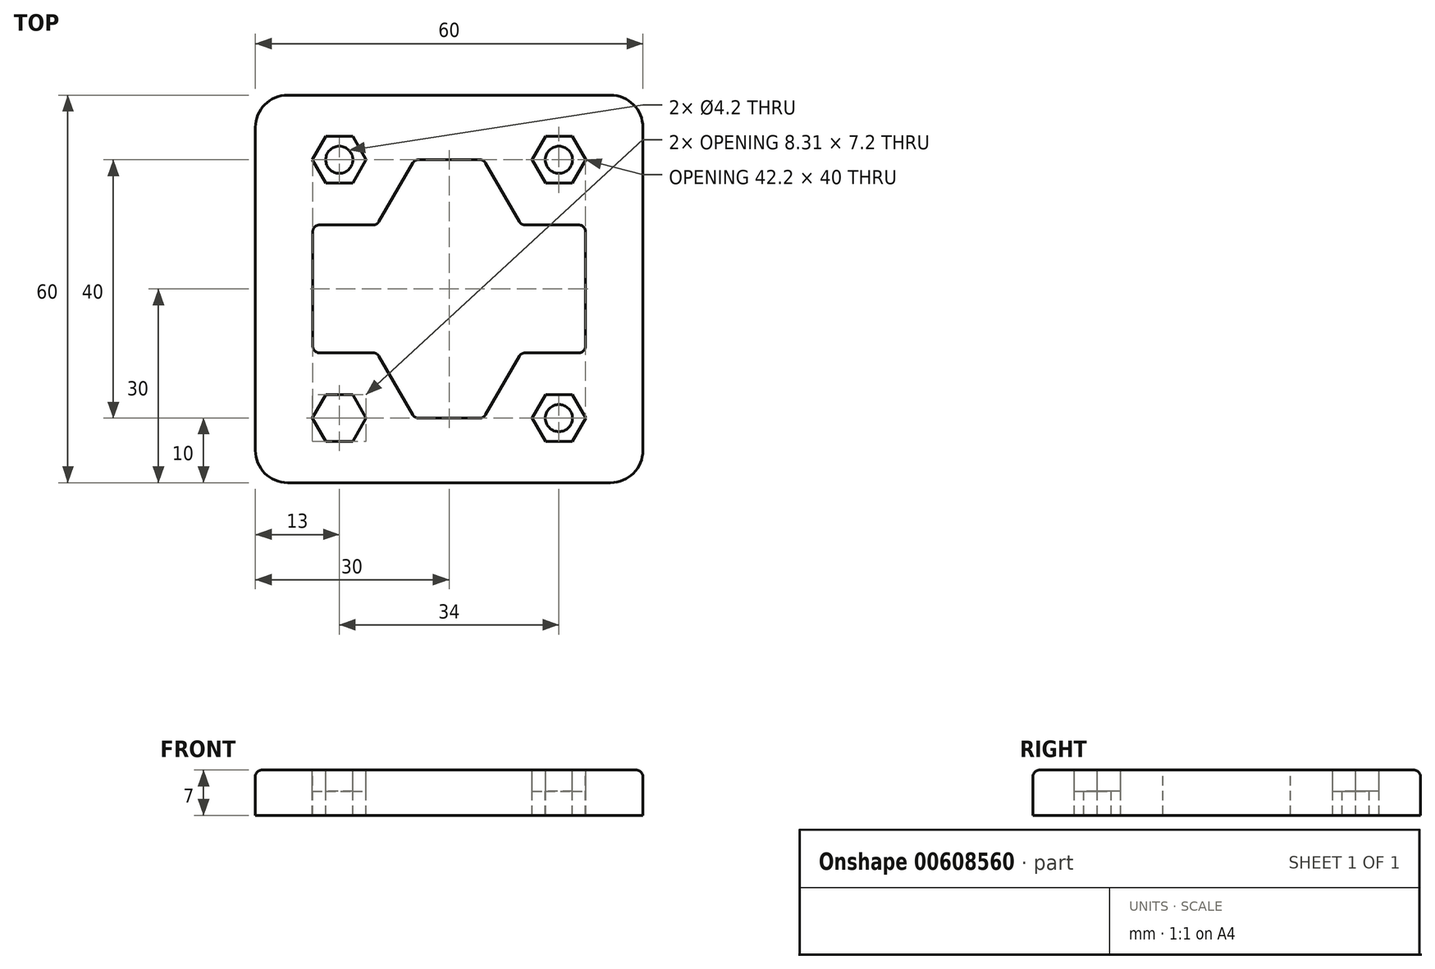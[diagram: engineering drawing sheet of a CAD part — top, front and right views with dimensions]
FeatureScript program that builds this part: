
annotation { "Feature Type Name" : "Feature", "Feature Type Description" : "" }
export const myFeature = defineFeature(function(context is Context, id is Id, definition is map)
    precondition{}
    {
        {
            var Q0;
            Q0=qCreatedBy(makeId("Top.planeOp"),FACE);
            var sketch = newSketch(context, id + "F0", { "sketchPlane" : qUnion([Q0])});
            skLineSegment(sketch, "E0.bottom", {"start": v(30, 30) * mm, "end": v(-30, 30) * mm});
            skLineSegment(sketch, "E0.top", {"start": v(30, -30) * mm, "end": v(-30, -30) * mm});
            skLineSegment(sketch, "E0.left", {"start": v(30, 30) * mm, "end": v(30, -30) * mm});
            skLineSegment(sketch, "E0.right", {"start": v(-30, 30) * mm, "end": v(-30, -30) * mm});
            skPoint(sketch, "E0.middle", {"position": v(0, 0) * mm});
            skSolve(sketch);
        }
        {
            var Q0;
            Q0=makeQuery(id+"F0.imprint","IMPRINT",FACE,{"disambiguationData":[TD([[makeQuery(id+"F0.imprint","IMPRINT",EDGE,{"derivedFrom":sQuery(id+"F0.wireOp",EDGE,"E0.bottom")}),1.0]])]});
            extrude(context, id + "F1", {"entities" : qUnion([Q0]), "oppositeDirection" : true, "depth" : 7 * mm, "offsetDistance" : 25 * mm});
        }
        {
            var Q0;
            Q0=makeQuery(id+"F1.opExtrude","SWEPT_EDGE",EDGE,{"disambiguationData":[OSD([sQuery(id+"F0.wireOp",EDGE,"E0.bottom"),sQuery(id+"F0.wireOp",EDGE,"E0.right")])]});
            var Q1;
            Q1=makeQuery(id+"F1.opExtrude","SWEPT_EDGE",EDGE,{"disambiguationData":[OSD([sQuery(id+"F0.wireOp",EDGE,"E0.bottom"),sQuery(id+"F0.wireOp",EDGE,"E0.left")])]});
            var Q2;
            Q2=makeQuery(id+"F1.opExtrude","SWEPT_EDGE",EDGE,{"disambiguationData":[OSD([sQuery(id+"F0.wireOp",EDGE,"E0.top"),sQuery(id+"F0.wireOp",EDGE,"E0.left")])]});
            var Q3;
            Q3=makeQuery(id+"F1.opExtrude","SWEPT_EDGE",EDGE,{"disambiguationData":[OSD([sQuery(id+"F0.wireOp",EDGE,"E0.top"),sQuery(id+"F0.wireOp",EDGE,"E0.right")])]});
            fillet(context, id + "F2", {"entities" : qUnion([Q0, Q1, Q2, Q3]), "radius" : 5 * mm, "tangentPropagation" : true, "allowEdgeOverflow" : false});
        }
        {
            var Q0;
            Q0=makeQuery(id+"F1.opExtrude","CAP_FACE",FACE,{"disambiguationData":[OSD([sQuery(id+"F0.wireOp",EDGE,"E0.bottom"),sQuery(id+"F0.wireOp",EDGE,"E0.top"),sQuery(id+"F0.wireOp",EDGE,"E0.left"),sQuery(id+"F0.wireOp",EDGE,"E0.right")])],"isStart":true});
            var sketch = newSketch(context, id + "F3", { "sketchPlane" : qUnion([Q0])});
            skLineSegment(sketch, "E1", {"start": v(0, 0) * mm, "end": v(0, 20) * mm, "construction": true});
            skLineSegment(sketch, "E2", {"start": v(0, 20) * mm, "end": v(-17, 20) * mm, "construction": true});
            skCircle(sketch, "E3", {"center": v(-17, 20) * mm, "radius": 2.1 * mm});
            skCircle(sketch, "E4.MirrorC", {"center": v(17, 20) * mm, "radius": 2.1 * mm});
            skCircle(sketch, "E5.MirrorC", {"center": v(-17, -20) * mm, "radius": 2.1 * mm});
            skCircle(sketch, "E6.MirrorC", {"center": v(17, -20) * mm, "radius": 2.1 * mm});
            skLineSegment(sketch, "E7.0", {"start": v(-6.2, 18.5) * mm, "end": v(-10.3, 11.4) * mm});
            skLineSegment(sketch, "E8", {"start": v(-6.2, 18.5) * mm, "end": v(-5.34, 20) * mm});
            skLineSegment(sketch, "E9.0", {"start": v(-12.9, 9.9) * mm, "end": v(-21.1, 9.9) * mm});
            skLineSegment(sketch, "E10", {"start": v(-10.3, 11.4) * mm, "end": v(-11.17, 9.9) * mm});
            skLineSegment(sketch, "E11", {"start": v(-11.17, 9.9) * mm, "end": v(-12.9, 9.9) * mm});
            skLineSegment(sketch, "E12", {"start": v(-21.1, 9.9) * mm, "end": v(-25.2, 9.9) * mm});
            skLineSegment(sketch, "E13", {"start": v(-25.2, 9.9) * mm, "end": v(-25.2, 0) * mm});
            skLineSegment(sketch, "E14", {"start": v(-5.34, 20) * mm, "end": v(0, 20) * mm});
            skLineSegment(sketch, "E15", {"start": v(0, 20) * mm, "end": v(-5.34, 20) * mm});
            skLineSegment(sketch, "E16.MirrorCS", {"start": v(6.2, 18.5) * mm, "end": v(5.34, 20) * mm});
            skLineSegment(sketch, "E17.MirrorCS", {"start": v(6.2, 18.5) * mm, "end": v(10.3, 11.4) * mm});
            skLineSegment(sketch, "E18.MirrorCS", {"start": v(10.3, 11.4) * mm, "end": v(11.17, 9.9) * mm});
            skLineSegment(sketch, "E19.MirrorCS", {"start": v(11.17, 9.9) * mm, "end": v(12.9, 9.9) * mm});
            skLineSegment(sketch, "E20.MirrorCS", {"start": v(12.9, 9.9) * mm, "end": v(21.1, 9.9) * mm});
            skLineSegment(sketch, "E21.MirrorCS", {"start": v(21.1, 9.9) * mm, "end": v(25.2, 9.9) * mm});
            skLineSegment(sketch, "E22.MirrorCS", {"start": v(25.2, 9.9) * mm, "end": v(25.2, 0) * mm});
            skLineSegment(sketch, "E23.MirrorCS", {"start": v(-25.2, -9.9) * mm, "end": v(-25.2, 0) * mm});
            skLineSegment(sketch, "E24.MirrorCS", {"start": v(-21.1, -9.9) * mm, "end": v(-25.2, -9.9) * mm});
            skLineSegment(sketch, "E25.MirrorCS", {"start": v(-12.9, -9.9) * mm, "end": v(-21.1, -9.9) * mm});
            skLineSegment(sketch, "E26.MirrorCS", {"start": v(-11.17, -9.9) * mm, "end": v(-12.9, -9.9) * mm});
            skLineSegment(sketch, "E27.MirrorCS", {"start": v(-10.3, -11.4) * mm, "end": v(-11.17, -9.9) * mm});
            skLineSegment(sketch, "E28.MirrorCS", {"start": v(-6.2, -18.5) * mm, "end": v(-10.3, -11.4) * mm});
            skLineSegment(sketch, "E29.MirrorCS", {"start": v(-6.2, -18.5) * mm, "end": v(-5.34, -20) * mm});
            skLineSegment(sketch, "E30.MirrorCS", {"start": v(6.2, -18.5) * mm, "end": v(5.34, -20) * mm});
            skLineSegment(sketch, "E31.MirrorCS", {"start": v(6.2, -18.5) * mm, "end": v(10.3, -11.4) * mm});
            skLineSegment(sketch, "E32.MirrorCS", {"start": v(10.3, -11.4) * mm, "end": v(11.17, -9.9) * mm});
            skLineSegment(sketch, "E33.MirrorCS", {"start": v(11.17, -9.9) * mm, "end": v(12.9, -9.9) * mm});
            skLineSegment(sketch, "E34.MirrorCS", {"start": v(12.9, -9.9) * mm, "end": v(21.1, -9.9) * mm});
            skLineSegment(sketch, "E35.MirrorCS", {"start": v(21.1, -9.9) * mm, "end": v(25.2, -9.9) * mm});
            skLineSegment(sketch, "E36.MirrorCS", {"start": v(25.2, -9.9) * mm, "end": v(25.2, 0) * mm});
            skLineSegment(sketch, "E37", {"start": v(-5.34, 20) * mm, "end": v(5.34, 20) * mm});
            skLineSegment(sketch, "E38", {"start": v(5.34, -20) * mm, "end": v(-5.34, -20) * mm});
            skLineSegment(sketch, "E39", {"start": v(-21.1, 9.9) * mm, "end": v(-21.1, -9.9) * mm});
            skLineSegment(sketch, "E40", {"start": v(21.1, 9.9) * mm, "end": v(21.1, -9.9) * mm});
            skLineSegment(sketch, "E41", {"start": v(-17, 23.6) * mm, "end": v(-17, 16.4) * mm});
            skCircle(sketch, "E42.cCircle", {"center": v(-17, 20) * mm, "radius": 3.6 * mm, "construction": true});
            skLineSegment(sketch, "E42.0", {"start": v(-19.08, 23.6) * mm, "end": v(-14.92, 23.6) * mm});
            skLineSegment(sketch, "E42.1", {"start": v(-14.92, 23.6) * mm, "end": v(-12.84, 20) * mm});
            skLineSegment(sketch, "E42.2", {"start": v(-12.84, 20) * mm, "end": v(-14.92, 16.4) * mm});
            skLineSegment(sketch, "E42.3", {"start": v(-14.92, 16.4) * mm, "end": v(-19.08, 16.4) * mm});
            skLineSegment(sketch, "E42.4", {"start": v(-19.08, 16.4) * mm, "end": v(-21.16, 20) * mm});
            skLineSegment(sketch, "E42.5", {"start": v(-21.16, 20) * mm, "end": v(-19.08, 23.6) * mm});
            skPoint(sketch, "E42.0.midPoint", {"position": v(-17, 23.6) * mm});
            skLineSegment(sketch, "E43.MirrorCS", {"start": v(14.92, 23.6) * mm, "end": v(12.84, 20) * mm});
            skLineSegment(sketch, "E44.MirrorCS", {"start": v(19.08, 23.6) * mm, "end": v(14.92, 23.6) * mm});
            skLineSegment(sketch, "E45.MirrorCS", {"start": v(21.16, 20) * mm, "end": v(19.08, 23.6) * mm});
            skLineSegment(sketch, "E46.MirrorCS", {"start": v(19.08, 16.4) * mm, "end": v(21.16, 20) * mm});
            skLineSegment(sketch, "E47.MirrorCS", {"start": v(14.92, 16.4) * mm, "end": v(19.08, 16.4) * mm});
            skLineSegment(sketch, "E48.MirrorCS", {"start": v(12.84, 20) * mm, "end": v(14.92, 16.4) * mm});
            skLineSegment(sketch, "E49.MirrorCS", {"start": v(-19.08, -23.6) * mm, "end": v(-14.92, -23.6) * mm});
            skLineSegment(sketch, "E50.MirrorCS", {"start": v(-21.16, -20) * mm, "end": v(-19.08, -23.6) * mm});
            skLineSegment(sketch, "E51.MirrorCS", {"start": v(-12.84, -20) * mm, "end": v(-14.92, -16.4) * mm});
            skLineSegment(sketch, "E52.MirrorCS", {"start": v(-14.92, -16.4) * mm, "end": v(-19.08, -16.4) * mm});
            skLineSegment(sketch, "E53.MirrorCS", {"start": v(-17, -23.6) * mm, "end": v(-17, -16.4) * mm});
            skLineSegment(sketch, "E54.MirrorCS", {"start": v(-19.08, -16.4) * mm, "end": v(-21.16, -20) * mm});
            skPoint(sketch, "E55.MirrorP", {"position": v(-17, -23.6) * mm});
            skCircle(sketch, "E56.MirrorC", {"center": v(-17, -20) * mm, "radius": 3.6 * mm, "construction": true});
            skLineSegment(sketch, "E57.MirrorCS", {"start": v(-14.92, -23.6) * mm, "end": v(-12.84, -20) * mm});
            skLineSegment(sketch, "E58.MirrorCS", {"start": v(21.16, -20) * mm, "end": v(19.08, -23.6) * mm});
            skLineSegment(sketch, "E59.MirrorCS", {"start": v(19.08, -16.4) * mm, "end": v(21.16, -20) * mm});
            skLineSegment(sketch, "E60.MirrorCS", {"start": v(12.84, -20) * mm, "end": v(14.92, -16.4) * mm});
            skLineSegment(sketch, "E61.MirrorCS", {"start": v(14.92, -23.6) * mm, "end": v(12.84, -20) * mm});
            skLineSegment(sketch, "E62.MirrorCS", {"start": v(14.92, -16.4) * mm, "end": v(19.08, -16.4) * mm});
            skLineSegment(sketch, "E63.MirrorCS", {"start": v(19.08, -23.6) * mm, "end": v(14.92, -23.6) * mm});
            skSolve(sketch);
        }
        {
            var Q0;
            Q0=makeQuery(id+"F3.imprint","IMPRINT",FACE,{"disambiguationData":[TD([[makeQuery(id+"F3.imprint","IMPRINT",EDGE,{"derivedFrom":sQuery(id+"F3.wireOp",EDGE,"E3")}),1.0]])]});
            var Q1;
            Q1=makeQuery(id+"F3.imprint","IMPRINT",FACE,{"disambiguationData":[TD([[makeQuery(id+"F3.imprint","IMPRINT",EDGE,{"derivedFrom":sQuery(id+"F3.wireOp",EDGE,"E4.MirrorC")}),-1.0]])]});
            var Q2;
            Q2=makeQuery(id+"F3.imprint","IMPRINT",FACE,{"disambiguationData":[TD([[makeQuery(id+"F3.imprint","IMPRINT",EDGE,{"derivedFrom":sQuery(id+"F3.wireOp",EDGE,"E6.MirrorC")}),1.0]])]});
            var Q3;
            Q3=makeQuery(id+"F3.imprint","IMPRINT",FACE,{"disambiguationData":[TD([[makeQuery(id+"F3.imprint","IMPRINT",EDGE,{"derivedFrom":sQuery(id+"F3.wireOp",EDGE,"E5.MirrorC")}),-1.0]])]});
            var Q4;
            {var subQ0=sQuery(id+"F3.wireOp",EDGE,"E5.MirrorC");var subQ1=sQuery(id+"F3.wireOp",EDGE,"E53.MirrorCS");var subQ2=makeQuery(id+"F3.imprint","INTERSECT",VERTEX,{"disambiguationData":[OD(0.0)],"derivedFrom":[subQ1,subQ0]});Q4=makeQuery(id+"F3.imprint","IMPRINT",FACE,{"disambiguationData":[TD([[makeQuery(id+"F3.imprint","IMPRINT",EDGE,{"disambiguationData":[TD([[subQ2,-1.0]])],"derivedFrom":subQ1}),1.0]])]});}
            var Q5;
            {var subQ0=sQuery(id+"F3.wireOp",EDGE,"E5.MirrorC");var subQ1=sQuery(id+"F3.wireOp",EDGE,"E53.MirrorCS");var subQ2=makeQuery(id+"F3.imprint","INTERSECT",VERTEX,{"disambiguationData":[OD(0.0)],"derivedFrom":[subQ1,subQ0]});Q5=makeQuery(id+"F3.imprint","IMPRINT",FACE,{"disambiguationData":[TD([[makeQuery(id+"F3.imprint","IMPRINT",EDGE,{"disambiguationData":[TD([[subQ2,-1.0]])],"derivedFrom":subQ1}),-1.0]])]});}
            var Q6;
            Q6=makeQuery(id+"F3.imprint","IMPRINT",FACE,{"disambiguationData":[TD([[makeQuery(id+"F3.imprint","IMPRINT",EDGE,{"derivedFrom":sQuery(id+"F3.wireOp",EDGE,"E6.MirrorC")}),1.0]])]});
            extrude(context, id + "F4", {"entities" : qUnion([Q0, Q1, Q2, Q3, Q4, Q5, Q6]), "operationType" : NewBodyOperationType.REMOVE, "oppositeDirection" : true, "depth" : 25 * mm, "offsetDistance" : 25 * mm});
        }
        {
            var Q0;
            Q0=makeQuery(id+"F3.imprint","IMPRINT",FACE,{"disambiguationData":[TD([[makeQuery(id+"F3.imprint","IMPRINT",EDGE,{"derivedFrom":sQuery(id+"F3.wireOp",EDGE,"E3")}),-1.0]])]});
            var Q1;
            Q1=makeQuery(id+"F3.imprint","IMPRINT",FACE,{"disambiguationData":[TD([[makeQuery(id+"F3.imprint","IMPRINT",EDGE,{"derivedFrom":sQuery(id+"F3.wireOp",EDGE,"E4.MirrorC")}),1.0]])]});
            var Q2;
            Q2=makeQuery(id+"F3.imprint","IMPRINT",FACE,{"disambiguationData":[TD([[makeQuery(id+"F3.imprint","IMPRINT",EDGE,{"derivedFrom":sQuery(id+"F3.wireOp",EDGE,"297063ce-58de-4e23-9618-ebe68274b3f90.MirrorCS")}),-1.0]])]});
            var Q3;
            Q3=makeQuery(id+"F3.imprint","IMPRINT",FACE,{"disambiguationData":[TD([[makeQuery(id+"F3.imprint","IMPRINT",EDGE,{"derivedFrom":sQuery(id+"F3.wireOp",EDGE,"11c745cf-a508-4151-a166-093f8a6f8d340.MirrorCS")}),1.0]])]});
            var Q4;
            {var subQ5=sQuery(id+"F3.wireOp",EDGE,"E50.MirrorCS");Q4=makeQuery(id+"F3.imprint","IMPRINT",FACE,{"disambiguationData":[TD([[makeQuery(id+"F3.imprint","IMPRINT",EDGE,{"derivedFrom":subQ5}),1.0]])]});}
            var Q5;
            {var subQ1=sQuery(id+"F3.wireOp",EDGE,"E51.MirrorCS");Q5=makeQuery(id+"F3.imprint","IMPRINT",FACE,{"disambiguationData":[TD([[makeQuery(id+"F3.imprint","IMPRINT",EDGE,{"derivedFrom":subQ1}),1.0]])]});}
            var Q6;
            Q6=makeQuery(id+"F3.imprint","IMPRINT",FACE,{"disambiguationData":[TD([[makeQuery(id+"F3.imprint","IMPRINT",EDGE,{"derivedFrom":sQuery(id+"F3.wireOp",EDGE,"E58.MirrorCS")}),-1.0]])]});
            extrude(context, id + "F5", {"entities" : qUnion([Q0, Q1, Q2, Q3, Q4, Q5, Q6]), "operationType" : NewBodyOperationType.REMOVE, "oppositeDirection" : true, "depth" : 3.3 * mm, "offsetDistance" : 25 * mm});
        }
        {
            var Q0;
            Q0=makeQuery(id+"F1.opExtrude","CAP_EDGE",EDGE,{"disambiguationData":[OSD([sQuery(id+"F0.wireOp",EDGE,"E0.left")])],"isStart":true});
            var Q1;
            Q1=makeQuery(id+"F1.opExtrude","CAP_EDGE",EDGE,{"disambiguationData":[OSD([sQuery(id+"F0.wireOp",EDGE,"E0.bottom")])],"isStart":true});
            var Q2;
            Q2=makeQuery(id+"F1.opExtrude","CAP_EDGE",EDGE,{"disambiguationData":[OSD([sQuery(id+"F0.wireOp",EDGE,"E0.right")])],"isStart":true});
            var Q3;
            Q3=makeQuery(id+"F1.opExtrude","CAP_EDGE",EDGE,{"disambiguationData":[OSD([sQuery(id+"F0.wireOp",EDGE,"E0.top")])],"isStart":true});
            var Q4;
            {var subQ0=sQuery(id+"F0.wireOp",EDGE,"E0.right");var subQ1=sQuery(id+"F0.wireOp",EDGE,"E0.top");Q4=makeQuery(id+"F2.opFillet","BLEND_EDGE",EDGE,{"blendedFrom":[makeQuery(id+"F1.opExtrude","SWEPT_EDGE",EDGE,{"disambiguationData":[OSD([subQ1,subQ0])]}),makeQuery(id+"F1.opExtrude","CAP_FACE",FACE,{"disambiguationData":[OSD([sQuery(id+"F0.wireOp",EDGE,"E0.bottom"),subQ1,sQuery(id+"F0.wireOp",EDGE,"E0.left"),subQ0])],"isStart":true})],"blendedInto":[makeQuery(id+"F1.opExtrude","CAP_FACE",FACE,{"disambiguationData":[OSD([sQuery(id+"F0.wireOp",EDGE,"E0.bottom"),subQ1,sQuery(id+"F0.wireOp",EDGE,"E0.left"),subQ0])],"isStart":true})]});}
            var Q5;
            {var subQ0=sQuery(id+"F0.wireOp",EDGE,"E0.left");var subQ1=sQuery(id+"F0.wireOp",EDGE,"E0.top");Q5=makeQuery(id+"F2.opFillet","BLEND_EDGE",EDGE,{"blendedFrom":[makeQuery(id+"F1.opExtrude","SWEPT_EDGE",EDGE,{"disambiguationData":[OSD([subQ1,subQ0])]}),makeQuery(id+"F1.opExtrude","CAP_FACE",FACE,{"disambiguationData":[OSD([sQuery(id+"F0.wireOp",EDGE,"E0.bottom"),subQ1,subQ0,sQuery(id+"F0.wireOp",EDGE,"E0.right")])],"isStart":true})],"blendedInto":[makeQuery(id+"F1.opExtrude","CAP_FACE",FACE,{"disambiguationData":[OSD([sQuery(id+"F0.wireOp",EDGE,"E0.bottom"),subQ1,subQ0,sQuery(id+"F0.wireOp",EDGE,"E0.right")])],"isStart":true})]});}
            var Q6;
            {var subQ0=sQuery(id+"F0.wireOp",EDGE,"E0.left");var subQ1=sQuery(id+"F0.wireOp",EDGE,"E0.bottom");Q6=makeQuery(id+"F2.opFillet","BLEND_EDGE",EDGE,{"blendedFrom":[makeQuery(id+"F1.opExtrude","SWEPT_EDGE",EDGE,{"disambiguationData":[OSD([subQ1,subQ0])]}),makeQuery(id+"F1.opExtrude","CAP_FACE",FACE,{"disambiguationData":[OSD([subQ1,sQuery(id+"F0.wireOp",EDGE,"E0.top"),subQ0,sQuery(id+"F0.wireOp",EDGE,"E0.right")])],"isStart":true})],"blendedInto":[makeQuery(id+"F1.opExtrude","CAP_FACE",FACE,{"disambiguationData":[OSD([subQ1,sQuery(id+"F0.wireOp",EDGE,"E0.top"),subQ0,sQuery(id+"F0.wireOp",EDGE,"E0.right")])],"isStart":true})]});}
            var Q7;
            {var subQ0=sQuery(id+"F0.wireOp",EDGE,"E0.right");var subQ1=sQuery(id+"F0.wireOp",EDGE,"E0.bottom");Q7=makeQuery(id+"F2.opFillet","BLEND_EDGE",EDGE,{"blendedFrom":[makeQuery(id+"F1.opExtrude","SWEPT_EDGE",EDGE,{"disambiguationData":[OSD([subQ1,subQ0])]}),makeQuery(id+"F1.opExtrude","CAP_FACE",FACE,{"disambiguationData":[OSD([subQ1,sQuery(id+"F0.wireOp",EDGE,"E0.top"),sQuery(id+"F0.wireOp",EDGE,"E0.left"),subQ0])],"isStart":true})],"blendedInto":[makeQuery(id+"F1.opExtrude","CAP_FACE",FACE,{"disambiguationData":[OSD([subQ1,sQuery(id+"F0.wireOp",EDGE,"E0.top"),sQuery(id+"F0.wireOp",EDGE,"E0.left"),subQ0])],"isStart":true})]});}
            fillet(context, id + "F6", {"entities" : qUnion([Q0, Q1, Q2, Q3, Q4, Q5, Q6, Q7]), "radius" : 1 * mm, "tangentPropagation" : true, "allowEdgeOverflow" : false});
        }
        {
            var Q0;
            Q0=makeQuery(id+"F3.imprint","IMPRINT",FACE,{"disambiguationData":[TD([[makeQuery(id+"F3.imprint","IMPRINT",EDGE,{"derivedFrom":sQuery(id+"F3.wireOp",EDGE,"E7.0")}),1.0]])]});
            extrude(context, id + "F7", {"entities" : qUnion([Q0]), "operationType" : NewBodyOperationType.REMOVE, "oppositeDirection" : true, "depth" : 25 * mm, "offsetDistance" : 25 * mm});
        }
        {
            var Q0;
            Q0=makeQuery(id+"F7.boolean.opBoolean","COPY",EDGE,{"derivedFrom":makeQuery(id+"F7.opExtrude","CAP_EDGE",EDGE,{"disambiguationData":[OSD([sQuery(id+"F3.wireOp",EDGE,"E9.0"),sQuery(id+"F3.wireOp",EDGE,"E11")])],"isStart":true})});
            var Q1;
            Q1=makeQuery(id+"F7.boolean.opBoolean","COPY",EDGE,{"derivedFrom":makeQuery(id+"F7.opExtrude","CAP_EDGE",EDGE,{"disambiguationData":[OSD([sQuery(id+"F3.wireOp",EDGE,"E39")])],"isStart":true})});
            var Q2;
            Q2=makeQuery(id+"F7.boolean.opBoolean","COPY",EDGE,{"derivedFrom":makeQuery(id+"F7.opExtrude","CAP_EDGE",EDGE,{"disambiguationData":[OSD([sQuery(id+"F3.wireOp",EDGE,"E7.0"),sQuery(id+"F3.wireOp",EDGE,"E8"),sQuery(id+"F3.wireOp",EDGE,"E10")])],"isStart":true})});
            var Q3;
            Q3=makeQuery(id+"F7.boolean.opBoolean","COPY",EDGE,{"derivedFrom":makeQuery(id+"F7.opExtrude","CAP_EDGE",EDGE,{"disambiguationData":[OSD([sQuery(id+"F3.wireOp",EDGE,"E37")])],"isStart":true})});
            var Q4;
            Q4=makeQuery(id+"F7.boolean.opBoolean","COPY",EDGE,{"derivedFrom":makeQuery(id+"F7.opExtrude","CAP_EDGE",EDGE,{"disambiguationData":[OSD([sQuery(id+"F3.wireOp",EDGE,"E16.MirrorCS"),sQuery(id+"F3.wireOp",EDGE,"E17.MirrorCS"),sQuery(id+"F3.wireOp",EDGE,"E18.MirrorCS")])],"isStart":true})});
            var Q5;
            Q5=makeQuery(id+"F7.boolean.opBoolean","COPY",EDGE,{"derivedFrom":makeQuery(id+"F7.opExtrude","CAP_EDGE",EDGE,{"disambiguationData":[OSD([sQuery(id+"F3.wireOp",EDGE,"E19.MirrorCS"),sQuery(id+"F3.wireOp",EDGE,"E20.MirrorCS")])],"isStart":true})});
            var Q6;
            Q6=makeQuery(id+"F7.boolean.opBoolean","COPY",EDGE,{"derivedFrom":makeQuery(id+"F7.opExtrude","CAP_EDGE",EDGE,{"disambiguationData":[OSD([sQuery(id+"F3.wireOp",EDGE,"E40")])],"isStart":true})});
            var Q7;
            Q7=makeQuery(id+"F7.boolean.opBoolean","COPY",EDGE,{"derivedFrom":makeQuery(id+"F7.opExtrude","CAP_EDGE",EDGE,{"disambiguationData":[OSD([sQuery(id+"F3.wireOp",EDGE,"E33.MirrorCS"),sQuery(id+"F3.wireOp",EDGE,"E34.MirrorCS")])],"isStart":true})});
            var Q8;
            Q8=makeQuery(id+"F7.boolean.opBoolean","COPY",EDGE,{"derivedFrom":makeQuery(id+"F7.opExtrude","CAP_EDGE",EDGE,{"disambiguationData":[OSD([sQuery(id+"F3.wireOp",EDGE,"E30.MirrorCS"),sQuery(id+"F3.wireOp",EDGE,"E31.MirrorCS"),sQuery(id+"F3.wireOp",EDGE,"E32.MirrorCS")])],"isStart":true})});
            var Q9;
            Q9=makeQuery(id+"F7.boolean.opBoolean","COPY",EDGE,{"derivedFrom":makeQuery(id+"F7.opExtrude","CAP_EDGE",EDGE,{"disambiguationData":[OSD([sQuery(id+"F3.wireOp",EDGE,"E38")])],"isStart":true})});
            var Q10;
            Q10=makeQuery(id+"F7.boolean.opBoolean","COPY",EDGE,{"derivedFrom":makeQuery(id+"F7.opExtrude","CAP_EDGE",EDGE,{"disambiguationData":[OSD([sQuery(id+"F3.wireOp",EDGE,"E27.MirrorCS"),sQuery(id+"F3.wireOp",EDGE,"E28.MirrorCS"),sQuery(id+"F3.wireOp",EDGE,"E29.MirrorCS")])],"isStart":true})});
            var Q11;
            Q11=makeQuery(id+"F7.boolean.opBoolean","COPY",EDGE,{"derivedFrom":makeQuery(id+"F7.opExtrude","CAP_EDGE",EDGE,{"disambiguationData":[OSD([sQuery(id+"F3.wireOp",EDGE,"E25.MirrorCS"),sQuery(id+"F3.wireOp",EDGE,"E26.MirrorCS")])],"isStart":true})});
            var Q12;
            Q12=makeQuery(id+"F7.boolean.opBoolean","COPY",EDGE,{"derivedFrom":makeQuery(id+"F7.opExtrude","SWEPT_EDGE",EDGE,{"disambiguationData":[OSD([sQuery(id+"F3.wireOp",EDGE,"E10"),sQuery(id+"F3.wireOp",EDGE,"E11")])]})});
            var Q13;
            Q13=makeQuery(id+"F7.boolean.opBoolean","COPY",EDGE,{"derivedFrom":makeQuery(id+"F7.opExtrude","SWEPT_EDGE",EDGE,{"disambiguationData":[OSD([sQuery(id+"F3.wireOp",EDGE,"E8"),sQuery(id+"F3.wireOp",EDGE,"E37")])]})});
            var Q14;
            Q14=makeQuery(id+"F7.boolean.opBoolean","COPY",EDGE,{"derivedFrom":makeQuery(id+"F7.opExtrude","SWEPT_EDGE",EDGE,{"disambiguationData":[OSD([sQuery(id+"F3.wireOp",EDGE,"E16.MirrorCS"),sQuery(id+"F3.wireOp",EDGE,"E37")])]})});
            var Q15;
            Q15=makeQuery(id+"F7.boolean.opBoolean","COPY",EDGE,{"derivedFrom":makeQuery(id+"F7.opExtrude","SWEPT_EDGE",EDGE,{"disambiguationData":[OSD([sQuery(id+"F3.wireOp",EDGE,"E18.MirrorCS"),sQuery(id+"F3.wireOp",EDGE,"E19.MirrorCS")])]})});
            var Q16;
            Q16=makeQuery(id+"F7.boolean.opBoolean","COPY",EDGE,{"derivedFrom":makeQuery(id+"F7.opExtrude","SWEPT_EDGE",EDGE,{"disambiguationData":[OSD([sQuery(id+"F3.wireOp",EDGE,"E20.MirrorCS"),sQuery(id+"F3.wireOp",EDGE,"E21.MirrorCS"),sQuery(id+"F3.wireOp",EDGE,"E40")])]})});
            var Q17;
            Q17=makeQuery(id+"F7.boolean.opBoolean","COPY",EDGE,{"derivedFrom":makeQuery(id+"F7.opExtrude","SWEPT_EDGE",EDGE,{"disambiguationData":[OSD([sQuery(id+"F3.wireOp",EDGE,"E34.MirrorCS"),sQuery(id+"F3.wireOp",EDGE,"E35.MirrorCS"),sQuery(id+"F3.wireOp",EDGE,"E40")])]})});
            var Q18;
            Q18=makeQuery(id+"F7.boolean.opBoolean","COPY",EDGE,{"derivedFrom":makeQuery(id+"F7.opExtrude","SWEPT_EDGE",EDGE,{"disambiguationData":[OSD([sQuery(id+"F3.wireOp",EDGE,"E32.MirrorCS"),sQuery(id+"F3.wireOp",EDGE,"E33.MirrorCS")])]})});
            var Q19;
            Q19=makeQuery(id+"F7.boolean.opBoolean","COPY",EDGE,{"derivedFrom":makeQuery(id+"F7.opExtrude","SWEPT_EDGE",EDGE,{"disambiguationData":[OSD([sQuery(id+"F3.wireOp",EDGE,"E30.MirrorCS"),sQuery(id+"F3.wireOp",EDGE,"E38")])]})});
            var Q20;
            Q20=makeQuery(id+"F7.boolean.opBoolean","COPY",EDGE,{"derivedFrom":makeQuery(id+"F7.opExtrude","SWEPT_EDGE",EDGE,{"disambiguationData":[OSD([sQuery(id+"F3.wireOp",EDGE,"E29.MirrorCS"),sQuery(id+"F3.wireOp",EDGE,"E38")])]})});
            var Q21;
            Q21=makeQuery(id+"F7.boolean.opBoolean","COPY",EDGE,{"derivedFrom":makeQuery(id+"F7.opExtrude","SWEPT_EDGE",EDGE,{"disambiguationData":[OSD([sQuery(id+"F3.wireOp",EDGE,"E26.MirrorCS"),sQuery(id+"F3.wireOp",EDGE,"E27.MirrorCS")])]})});
            var Q22;
            Q22=makeQuery(id+"F7.boolean.opBoolean","COPY",EDGE,{"derivedFrom":makeQuery(id+"F7.opExtrude","SWEPT_EDGE",EDGE,{"disambiguationData":[OSD([sQuery(id+"F3.wireOp",EDGE,"E24.MirrorCS"),sQuery(id+"F3.wireOp",EDGE,"E25.MirrorCS"),sQuery(id+"F3.wireOp",EDGE,"E39")])]})});
            var Q23;
            Q23=makeQuery(id+"F7.boolean.opBoolean","COPY",EDGE,{"derivedFrom":makeQuery(id+"F7.opExtrude","SWEPT_EDGE",EDGE,{"disambiguationData":[OSD([sQuery(id+"F3.wireOp",EDGE,"E9.0"),sQuery(id+"F3.wireOp",EDGE,"E12"),sQuery(id+"F3.wireOp",EDGE,"E39")])]})});
            fillet(context, id + "F8", {"entities" : qUnion([Q0, Q1, Q2, Q3, Q4, Q5, Q6, Q7, Q8, Q9, Q10, Q11, Q12, Q13, Q14, Q15, Q16, Q17, Q18, Q19, Q20, Q21, Q22, Q23]), "radius" : 1 * mm, "tangentPropagation" : true, "allowEdgeOverflow" : false});
        }
    });
